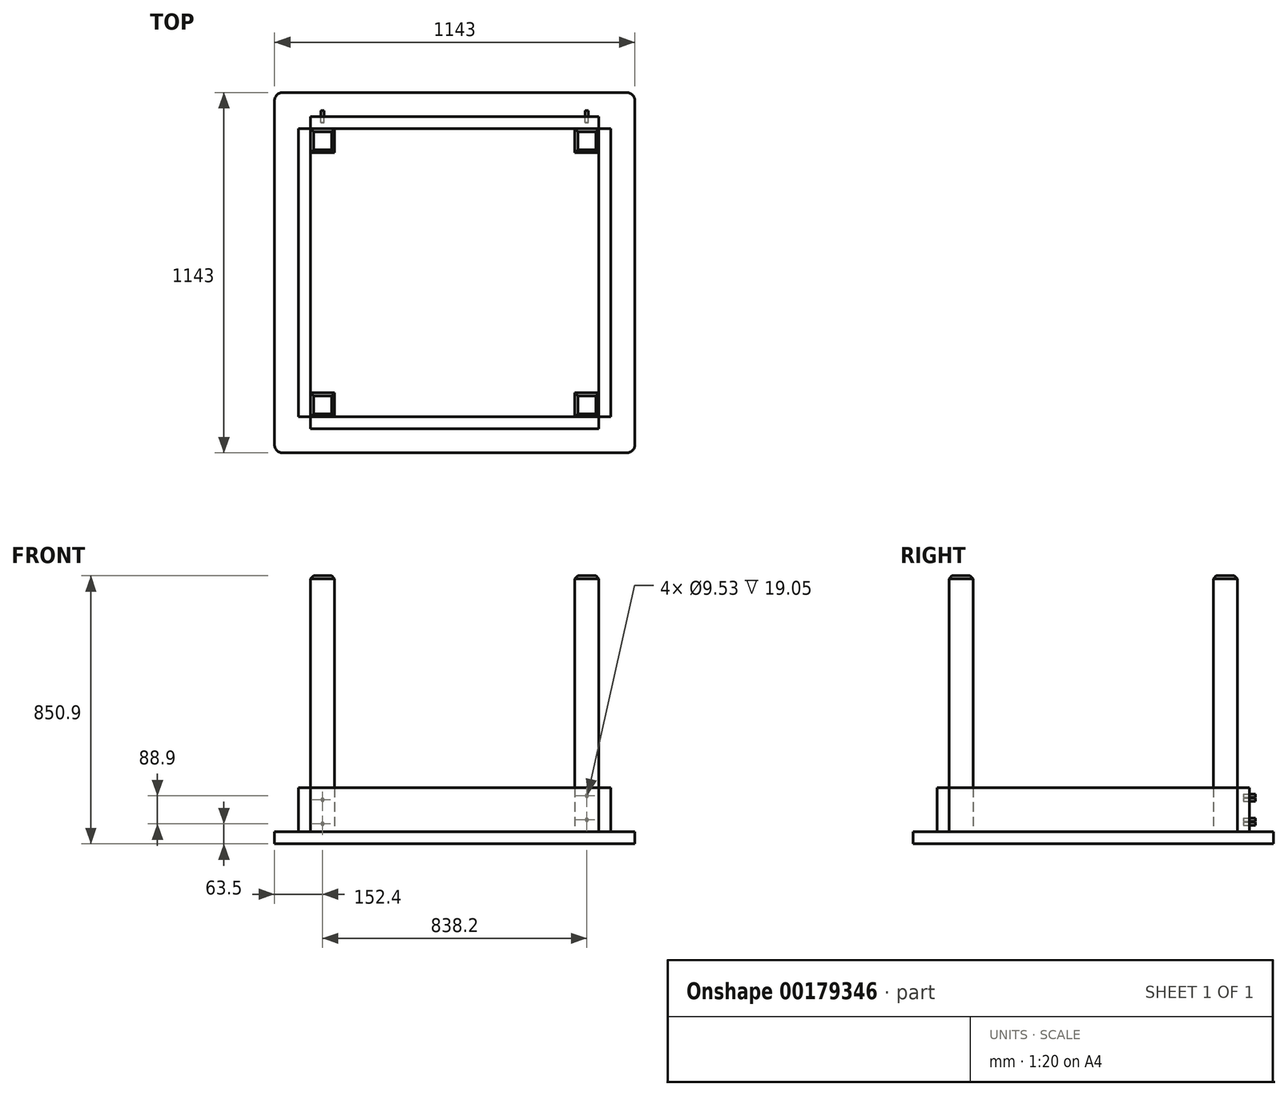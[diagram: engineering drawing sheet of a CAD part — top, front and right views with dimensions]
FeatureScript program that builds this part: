
annotation { "Feature Type Name" : "Feature", "Feature Type Description" : "" }
export const myFeature = defineFeature(function(context is Context, id is Id, definition is map)
    precondition{}
    {
        {
            var Q0;
            Q0=qCreatedBy(makeId("Top.planeOp"),FACE);
            var sketch = newSketch(context, id + "F0", { "sketchPlane" : qUnion([Q0])});
            skLineSegment(sketch, "E0.bottom", {"start": v(0, 0) * mm, "end": v(1143, 0) * mm});
            skLineSegment(sketch, "E0.top", {"start": v(0, 1143) * mm, "end": v(1143, 1143) * mm});
            skLineSegment(sketch, "E0.left", {"start": v(0, 0) * mm, "end": v(0, 1143) * mm});
            skLineSegment(sketch, "E0.right", {"start": v(1143, 0) * mm, "end": v(1143, 1143) * mm});
            skSolve(sketch);
        }
        {
            var Q0;
            Q0=makeQuery(id+"F0.imprint","IMPRINT",FACE,{"disambiguationData":[TD([[makeQuery(id+"F0.imprint","IMPRINT",EDGE,{"derivedFrom":sQuery(id+"F0.wireOp",EDGE,"E0.bottom")}),1.0]])]});
            extrude(context, id + "F1", {"entities" : qUnion([Q0]), "depth" : 38.1 * mm});
        }
        {
            var Q0;
            Q0=makeQuery(id+"F1.opExtrude","SWEPT_EDGE",EDGE,{"disambiguationData":[OSD([sQuery(id+"F0.wireOp",EDGE,"E0.bottom"),sQuery(id+"F0.wireOp",EDGE,"E0.left")])]});
            var Q1;
            Q1=makeQuery(id+"F1.opExtrude","SWEPT_EDGE",EDGE,{"disambiguationData":[OSD([sQuery(id+"F0.wireOp",EDGE,"E0.bottom"),sQuery(id+"F0.wireOp",EDGE,"E0.right")])]});
            var Q2;
            Q2=makeQuery(id+"F1.opExtrude","SWEPT_EDGE",EDGE,{"disambiguationData":[OSD([sQuery(id+"F0.wireOp",EDGE,"E0.top"),sQuery(id+"F0.wireOp",EDGE,"E0.left")])]});
            var Q3;
            Q3=makeQuery(id+"F1.opExtrude","SWEPT_EDGE",EDGE,{"disambiguationData":[OSD([sQuery(id+"F0.wireOp",EDGE,"E0.top"),sQuery(id+"F0.wireOp",EDGE,"E0.right")])]});
            fillet(context, id + "F2", {"entities" : qUnion([Q0, Q1, Q2, Q3]), "radius" : 25.4 * mm, "tangentPropagation" : true, "allowEdgeOverflow" : false});
        }
        {
            var Q0;
            Q0=makeQuery(id+"F1.opExtrude","CAP_FACE",FACE,{"disambiguationData":[OSD([sQuery(id+"F0.wireOp",EDGE,"E0.bottom"),sQuery(id+"F0.wireOp",EDGE,"E0.top"),sQuery(id+"F0.wireOp",EDGE,"E0.left"),sQuery(id+"F0.wireOp",EDGE,"E0.right")])],"isStart":false});
            var sketch = newSketch(context, id + "F3", { "sketchPlane" : qUnion([Q0])});
            skLineSegment(sketch, "E1.bottom", {"start": v(114.3, 114.3) * mm, "end": v(1028.7, 114.3) * mm, "construction": true});
            skLineSegment(sketch, "E1.top", {"start": v(114.3, 1028.7) * mm, "end": v(1028.7, 1028.7) * mm, "construction": true});
            skLineSegment(sketch, "E1.left", {"start": v(114.3, 114.3) * mm, "end": v(114.3, 1028.7) * mm, "construction": true});
            skLineSegment(sketch, "E1.right", {"start": v(1028.7, 114.3) * mm, "end": v(1028.7, 1028.7) * mm, "construction": true});
            skLineSegment(sketch, "E2.bottom", {"start": v(114.3, 114.3) * mm, "end": v(190.5, 114.3) * mm});
            skLineSegment(sketch, "E2.top", {"start": v(114.3, 190.5) * mm, "end": v(190.5, 190.5) * mm});
            skLineSegment(sketch, "E2.left", {"start": v(114.3, 114.3) * mm, "end": v(114.3, 190.5) * mm});
            skLineSegment(sketch, "E2.right", {"start": v(190.5, 114.3) * mm, "end": v(190.5, 190.5) * mm});
            skLineSegment(sketch, "E3", {"start": v(571.5, 114.3) * mm, "end": v(571.5, 1028.7) * mm, "construction": true});
            skLineSegment(sketch, "E4", {"start": v(114.3, 571.5) * mm, "end": v(1028.7, 571.5) * mm, "construction": true});
            skLineSegment(sketch, "E5.MirrorCS", {"start": v(952.5, 114.3) * mm, "end": v(952.5, 190.5) * mm});
            skLineSegment(sketch, "E6.MirrorCS", {"start": v(1028.7, 190.5) * mm, "end": v(952.5, 190.5) * mm});
            skLineSegment(sketch, "E7.MirrorCS", {"start": v(1028.7, 114.3) * mm, "end": v(952.5, 114.3) * mm});
            skLineSegment(sketch, "E8.MirrorCS", {"start": v(1028.7, 114.3) * mm, "end": v(1028.7, 190.5) * mm});
            skLineSegment(sketch, "E9.MirrorCS", {"start": v(1028.7, 571.5) * mm, "end": v(114.3, 571.5) * mm, "construction": true});
            skLineSegment(sketch, "E10.MirrorCS", {"start": v(1028.7, 1028.7) * mm, "end": v(952.5, 1028.7) * mm});
            skLineSegment(sketch, "E11.MirrorCS", {"start": v(1028.7, 1028.7) * mm, "end": v(1028.7, 952.5) * mm});
            skLineSegment(sketch, "E12.MirrorCS", {"start": v(1028.7, 952.5) * mm, "end": v(952.5, 952.5) * mm});
            skLineSegment(sketch, "E13.MirrorCS", {"start": v(952.5, 1028.7) * mm, "end": v(952.5, 952.5) * mm});
            skLineSegment(sketch, "E14.MirrorCS", {"start": v(114.3, 1028.7) * mm, "end": v(190.5, 1028.7) * mm});
            skLineSegment(sketch, "E15.MirrorCS", {"start": v(114.3, 1028.7) * mm, "end": v(114.3, 952.5) * mm});
            skLineSegment(sketch, "E16.MirrorCS", {"start": v(190.5, 1028.7) * mm, "end": v(190.5, 952.5) * mm});
            skLineSegment(sketch, "E17.MirrorCS", {"start": v(114.3, 952.5) * mm, "end": v(190.5, 952.5) * mm});
            skSolve(sketch);
        }
        {
            var Q0;
            Q0=makeQuery(id+"F3.imprint","IMPRINT",FACE,{"disambiguationData":[TD([[makeQuery(id+"F3.imprint","IMPRINT",EDGE,{"derivedFrom":sQuery(id+"F3.wireOp",EDGE,"E2.bottom")}),1.0]])]});
            var Q1;
            Q1=makeQuery(id+"F3.imprint","IMPRINT",FACE,{"disambiguationData":[TD([[makeQuery(id+"F3.imprint","IMPRINT",EDGE,{"derivedFrom":sQuery(id+"F3.wireOp",EDGE,"E14.MirrorCS")}),-1.0]])]});
            var Q2;
            Q2=makeQuery(id+"F3.imprint","IMPRINT",FACE,{"disambiguationData":[TD([[makeQuery(id+"F3.imprint","IMPRINT",EDGE,{"derivedFrom":sQuery(id+"F3.wireOp",EDGE,"E5.MirrorCS")}),-1.0]])]});
            var Q3;
            Q3=makeQuery(id+"F3.imprint","IMPRINT",FACE,{"disambiguationData":[TD([[makeQuery(id+"F3.imprint","IMPRINT",EDGE,{"derivedFrom":sQuery(id+"F3.wireOp",EDGE,"E10.MirrorCS")}),1.0]])]});
            extrude(context, id + "F4", {"entities" : qUnion([Q0, Q1, Q2, Q3]), "depth" : 812.8 * mm});
        }
        {
            var Q0;
            Q0=makeQuery(id+"F1.opExtrude","CAP_FACE",FACE,{"disambiguationData":[OSD([sQuery(id+"F0.wireOp",EDGE,"E0.bottom"),sQuery(id+"F0.wireOp",EDGE,"E0.top"),sQuery(id+"F0.wireOp",EDGE,"E0.left"),sQuery(id+"F0.wireOp",EDGE,"E0.right")])],"isStart":false});
            var sketch = newSketch(context, id + "F5", { "sketchPlane" : qUnion([Q0])});
            skLineSegment(sketch, "E18.bottom", {"start": v(114.3, 1028.7) * mm, "end": v(76.2, 1028.7) * mm});
            skLineSegment(sketch, "E18.top", {"start": v(114.3, 114.3) * mm, "end": v(76.2, 114.3) * mm});
            skLineSegment(sketch, "E18.left", {"start": v(114.3, 1028.7) * mm, "end": v(114.3, 114.3) * mm});
            skLineSegment(sketch, "E18.right", {"start": v(76.2, 1028.7) * mm, "end": v(76.2, 114.3) * mm});
            skLineSegment(sketch, "E19", {"start": v(571.5, 1143) * mm, "end": v(571.5, 0) * mm, "construction": true});
            skPoint(sketch, "E20", {"position": v(571.5, 571.5) * mm});
            skLineSegment(sketch, "E21.MirrorCS", {"start": v(1028.7, 114.3) * mm, "end": v(1066.8, 114.3) * mm});
            skLineSegment(sketch, "E22.MirrorCS", {"start": v(1028.7, 1028.7) * mm, "end": v(1028.7, 114.3) * mm});
            skLineSegment(sketch, "E23.MirrorCS", {"start": v(1028.7, 1028.7) * mm, "end": v(1066.8, 1028.7) * mm});
            skLineSegment(sketch, "E24.MirrorCS", {"start": v(1066.8, 1028.7) * mm, "end": v(1066.8, 114.3) * mm});
            skSolve(sketch);
        }
        {
            var Q0;
            {var subQ1=sQuery(id+"F5.wireOp",EDGE,"E18.bottom");Q0=makeQuery(id+"F5.imprint","IMPRINT",FACE,{"disambiguationData":[TD([[makeQuery(id+"F5.imprint","IMPRINT",EDGE,{"derivedFrom":subQ1}),1.0]])]});}
            var Q1;
            Q1=makeQuery(id+"F5.imprint","IMPRINT",FACE,{"disambiguationData":[TD([[makeQuery(id+"F5.imprint","IMPRINT",EDGE,{"derivedFrom":sQuery(id+"F5.wireOp",EDGE,"E21.MirrorCS")}),1.0]])]});
            extrude(context, id + "F6", {"entities" : qUnion([Q0, Q1]), "depth" : 139.7 * mm});
        }
        {
            var Q0;
            Q0=makeQuery(id+"F5.imprint","IMPRINT",FACE,{"disambiguationData":[TD([[makeQuery(id+"F5.imprint","IMPRINT",EDGE,{"derivedFrom":sQuery(id+"F5.wireOp",EDGE,"E18.bottom")}),-1.0]])]});
            var sketch = newSketch(context, id + "F7", { "sketchPlane" : qUnion([Q0])});
            skLineSegment(sketch, "E25.bottom", {"start": v(114.3, 1066.8) * mm, "end": v(1028.7, 1066.8) * mm});
            skLineSegment(sketch, "E25.top", {"start": v(114.3, 1028.7) * mm, "end": v(1028.7, 1028.7) * mm});
            skLineSegment(sketch, "E25.left", {"start": v(114.3, 1066.8) * mm, "end": v(114.3, 1028.7) * mm});
            skLineSegment(sketch, "E25.right", {"start": v(1028.7, 1066.8) * mm, "end": v(1028.7, 1028.7) * mm});
            skLineSegment(sketch, "E26.bottom", {"start": v(1028.7, 114.3) * mm, "end": v(114.3, 114.3) * mm});
            skLineSegment(sketch, "E26.top", {"start": v(1028.7, 76.2) * mm, "end": v(114.3, 76.2) * mm});
            skLineSegment(sketch, "E26.left", {"start": v(1028.7, 114.3) * mm, "end": v(1028.7, 76.2) * mm});
            skLineSegment(sketch, "E26.right", {"start": v(114.3, 114.3) * mm, "end": v(114.3, 76.2) * mm});
            skSolve(sketch);
        }
        {
            var Q0;
            Q0=makeQuery(id+"F7.imprint","IMPRINT",FACE,{"disambiguationData":[TD([[makeQuery(id+"F7.imprint","IMPRINT",EDGE,{"derivedFrom":sQuery(id+"F7.wireOp",EDGE,"E26.bottom")}),1.0]])]});
            var Q1;
            Q1=makeQuery(id+"F7.imprint","IMPRINT",FACE,{"disambiguationData":[TD([[makeQuery(id+"F7.imprint","IMPRINT",EDGE,{"derivedFrom":sQuery(id+"F7.wireOp",EDGE,"E25.bottom")}),-1.0]])]});
            extrude(context, id + "F8", {"entities" : qUnion([Q0, Q1]), "depth" : 139.7 * mm});
        }
        {
            var Q0;
            Q0=makeQuery(id+"F4.opExtrude","CAP_FACE",FACE,{"disambiguationData":[OSD([sQuery(id+"F3.wireOp",EDGE,"E14.MirrorCS"),sQuery(id+"F3.wireOp",EDGE,"E15.MirrorCS"),sQuery(id+"F3.wireOp",EDGE,"E16.MirrorCS"),sQuery(id+"F3.wireOp",EDGE,"E17.MirrorCS")])],"isStart":false});
            var Q1;
            Q1=makeQuery(id+"F4.opExtrude","CAP_FACE",FACE,{"disambiguationData":[OSD([sQuery(id+"F3.wireOp",EDGE,"E10.MirrorCS"),sQuery(id+"F3.wireOp",EDGE,"E11.MirrorCS"),sQuery(id+"F3.wireOp",EDGE,"E12.MirrorCS"),sQuery(id+"F3.wireOp",EDGE,"E13.MirrorCS")])],"isStart":false});
            var Q2;
            Q2=makeQuery(id+"F4.opExtrude","CAP_FACE",FACE,{"disambiguationData":[OSD([sQuery(id+"F3.wireOp",EDGE,"E2.bottom"),sQuery(id+"F3.wireOp",EDGE,"E2.top"),sQuery(id+"F3.wireOp",EDGE,"E2.left"),sQuery(id+"F3.wireOp",EDGE,"E2.right")])],"isStart":false});
            var Q3;
            Q3=makeQuery(id+"F4.opExtrude","CAP_FACE",FACE,{"disambiguationData":[OSD([sQuery(id+"F3.wireOp",EDGE,"E5.MirrorCS"),sQuery(id+"F3.wireOp",EDGE,"E6.MirrorCS"),sQuery(id+"F3.wireOp",EDGE,"E7.MirrorCS"),sQuery(id+"F3.wireOp",EDGE,"E8.MirrorCS")])],"isStart":false});
            chamfer(context, id + "F9", {"entities" : qUnion([Q0, Q1, Q2, Q3]), "width" : 9.52 * mm, "tangentPropagation" : true});
        }
        {
            var Q0;
            Q0=makeQuery(id+"F1.opExtrude","CAP_FACE",FACE,{"disambiguationData":[OSD([sQuery(id+"F0.wireOp",EDGE,"E0.bottom"),sQuery(id+"F0.wireOp",EDGE,"E0.top"),sQuery(id+"F0.wireOp",EDGE,"E0.left"),sQuery(id+"F0.wireOp",EDGE,"E0.right")])],"isStart":true});
            var sketch = newSketch(context, id + "F10", { "sketchPlane" : qUnion([Q0])});
            skCircle(sketch, "E27", {"center": v(571.5, -571.5) * mm, "radius": 254 * mm, "construction": true});
            skSolve(sketch);
        }
        {
            var Q0;
            Q0=makeQuery(id+"F8.opExtrude","SWEPT_FACE",FACE,{"disambiguationData":[OSD([sQuery(id+"F7.wireOp",EDGE,"E25.bottom")])]});
            var sketch = newSketch(context, id + "F11", { "sketchPlane" : qUnion([Q0])});
            skCircle(sketch, "E28", {"center": v(-152.4, 139.7) * mm, "radius": 4.76 * mm});
            skCircle(sketch, "E29", {"center": v(-152.4, 63.5) * mm, "radius": 4.76 * mm});
            skCircle(sketch, "E30", {"center": v(-990.6, 152.4) * mm, "radius": 4.76 * mm});
            skCircle(sketch, "E31", {"center": v(-990.6, 76.2) * mm, "radius": 4.76 * mm});
            skLineSegment(sketch, "E32", {"start": v(-152.4, 139.7) * mm, "end": v(-152.4, 63.5) * mm});
            skLineSegment(sketch, "E33", {"start": v(-990.6, 152.4) * mm, "end": v(-990.6, 76.2) * mm});
            skSolve(sketch);
        }
        {
            var Q0;
            Q0=makeQuery(id+"F11.imprint","IMPRINT",FACE,{"disambiguationData":[TD([[makeQuery(id+"F11.imprint","IMPRINT",EDGE,{"derivedFrom":sQuery(id+"F11.wireOp",EDGE,"E30")}),1.0]])]});
            var Q1;
            Q1=makeQuery(id+"F11.imprint","IMPRINT",FACE,{"disambiguationData":[TD([[makeQuery(id+"F11.imprint","IMPRINT",EDGE,{"derivedFrom":sQuery(id+"F11.wireOp",EDGE,"E31")}),1.0]])]});
            var Q2;
            Q2=makeQuery(id+"F11.imprint","IMPRINT",FACE,{"disambiguationData":[TD([[makeQuery(id+"F11.imprint","IMPRINT",EDGE,{"derivedFrom":sQuery(id+"F11.wireOp",EDGE,"E29")}),1.0]])]});
            var Q3;
            Q3=makeQuery(id+"F11.imprint","IMPRINT",FACE,{"disambiguationData":[TD([[makeQuery(id+"F11.imprint","IMPRINT",EDGE,{"derivedFrom":sQuery(id+"F11.wireOp",EDGE,"E28")}),1.0]])]});
            extrude(context, id + "F12", {"entities" : qUnion([Q0, Q1, Q2, Q3]), "endBound" : BoundingType.SYMMETRIC, "oppositeDirection" : true, "depth" : 38.1 * mm});
        }
        {
            var Q0;
            Q0=makeQuery(id+"F12.opExtrude","SWEPT_BODY",BODY,{"disambiguationData":[OSD([sQuery(id+"F11.wireOp",EDGE,"E29")])]});
            var Q1;
            Q1=makeQuery(id+"F12.opExtrude","SWEPT_BODY",BODY,{"disambiguationData":[OSD([sQuery(id+"F11.wireOp",EDGE,"E28")])]});
            var Q2;
            Q2=makeQuery(id+"F12.opExtrude","SWEPT_BODY",BODY,{"disambiguationData":[OSD([sQuery(id+"F11.wireOp",EDGE,"E30")])]});
            var Q3;
            Q3=makeQuery(id+"F12.opExtrude","SWEPT_BODY",BODY,{"disambiguationData":[OSD([sQuery(id+"F11.wireOp",EDGE,"E31")])]});
            var Q4;
            Q4=sQuery(id+"F10.wireOp",EDGE,"E27");
            circularPattern(context, id + "F13", {"entities" : qUnion([Q0, Q1, Q2, Q3]), "axis" : qUnion([Q4]), "angle" : 360 * degree, "instanceCount" : 4});
        }
        {
            var Q0;
            Q0=makeQuery(id+"F12.opExtrude","SWEPT_BODY",BODY,{"disambiguationData":[OSD([sQuery(id+"F11.wireOp",EDGE,"E29")])]});
            var Q1;
            Q1=makeQuery(id+"F12.opExtrude","SWEPT_BODY",BODY,{"disambiguationData":[OSD([sQuery(id+"F11.wireOp",EDGE,"E28")])]});
            var Q2;
            Q2=makeQuery(id+"F12.opExtrude","SWEPT_BODY",BODY,{"disambiguationData":[OSD([sQuery(id+"F11.wireOp",EDGE,"E31")])]});
            var Q3;
            Q3=makeQuery(id+"F12.opExtrude","SWEPT_BODY",BODY,{"disambiguationData":[OSD([sQuery(id+"F11.wireOp",EDGE,"E30")])]});
            var Q4;
            Q4=makeQuery(id+"F8.opExtrude","SWEPT_BODY",BODY,{"disambiguationData":[OSD([sQuery(id+"F7.wireOp",EDGE,"E25.bottom"),sQuery(id+"F7.wireOp",EDGE,"E25.top"),sQuery(id+"F7.wireOp",EDGE,"E25.left"),sQuery(id+"F7.wireOp",EDGE,"E25.right")])]});
            booleanBodies(context, id + "F14", {"operationType" : BooleanOperationType.SUBTRACTION, "tools" : qUnion([Q0, Q1, Q2, Q3]), "targets" : qUnion([Q4])});
        }
    });
